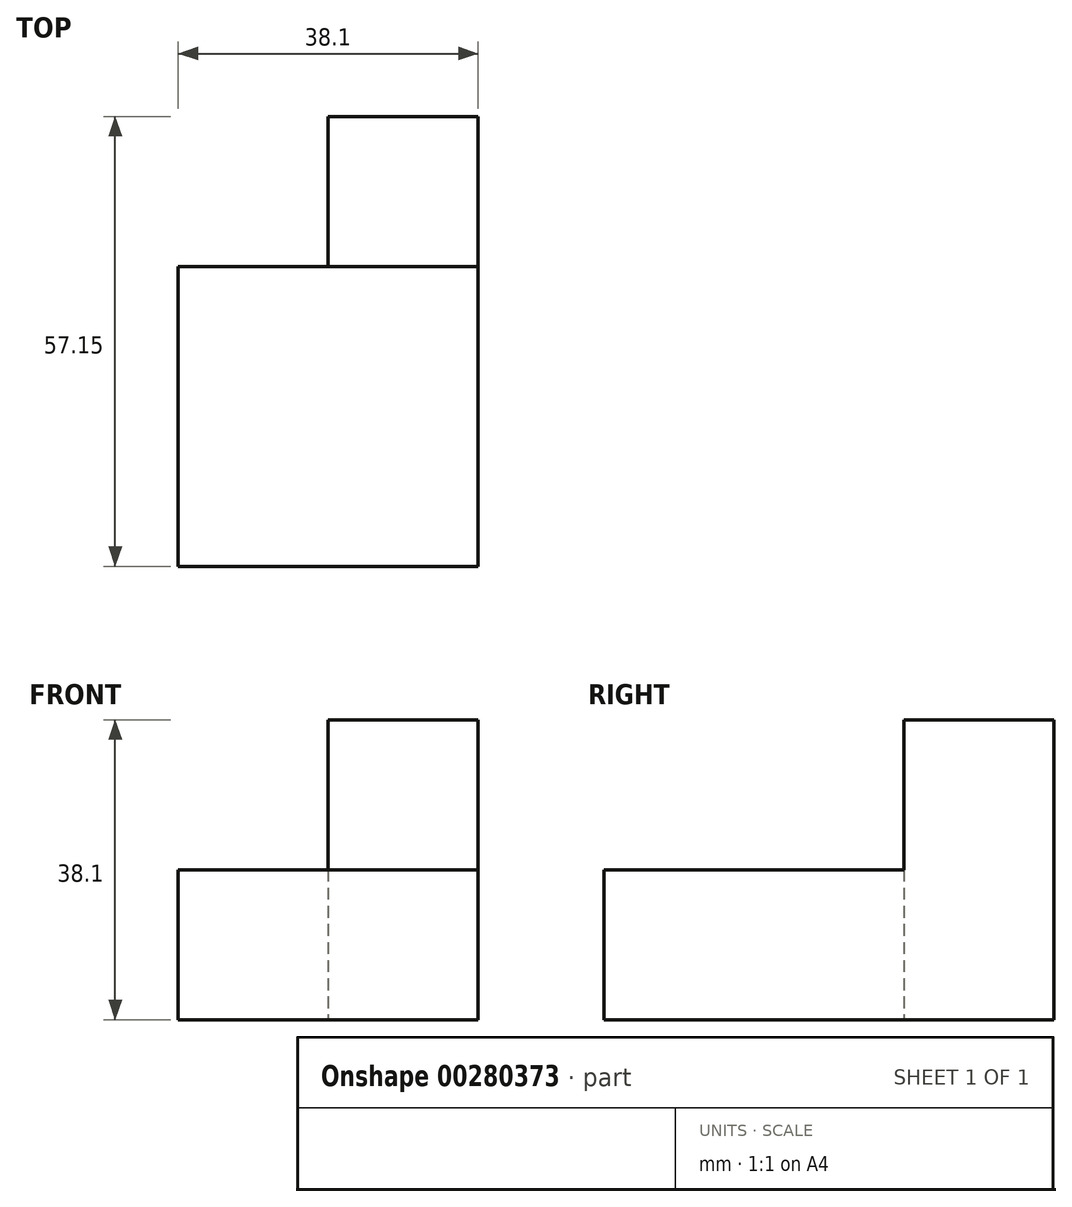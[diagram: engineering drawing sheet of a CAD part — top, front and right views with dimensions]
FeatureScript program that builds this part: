
annotation { "Feature Type Name" : "Feature", "Feature Type Description" : "" }
export const myFeature = defineFeature(function(context is Context, id is Id, definition is map)
    precondition{}
    {
        {
            var Q0;
            Q0=qCreatedBy(makeId("Top.planeOp"),FACE);
            var sketch = newSketch(context, id + "F0", { "sketchPlane" : qUnion([Q0])});
            skLineSegment(sketch, "E0.bottom", {"start": v(0, 0) * mm, "end": v(38.1, 0) * mm});
            skLineSegment(sketch, "E0.top", {"start": v(0, 38.1) * mm, "end": v(19.05, 38.1) * mm});
            skLineSegment(sketch, "E0.left", {"start": v(0, 0) * mm, "end": v(0, 38.1) * mm});
            skLineSegment(sketch, "E0.right", {"start": v(38.1, 0) * mm, "end": v(38.1, 38.1) * mm});
            skLineSegment(sketch, "E1", {"start": v(19.05, 38.1) * mm, "end": v(19.05, 57.15) * mm});
            skLineSegment(sketch, "E2", {"start": v(19.05, 57.15) * mm, "end": v(38.1, 57.15) * mm});
            skLineSegment(sketch, "E3", {"start": v(38.1, 57.15) * mm, "end": v(38.1, 38.1) * mm});
            skSolve(sketch);
        }
        {
            var Q0;
            Q0 = qSketchRegion(id + "F0", true);
            extrude(context, id + "F1", {"entities" : qUnion([Q0]), "depth" : 19.05 * mm});
        }
        {
            var Q0;
            Q0=makeQuery(id+"F1.opExtrude","CAP_FACE",FACE,{"disambiguationData":[OSD([sQuery(id+"F0.wireOp",EDGE,"E0.bottom"),sQuery(id+"F0.wireOp",EDGE,"E0.top"),sQuery(id+"F0.wireOp",EDGE,"E0.left"),sQuery(id+"F0.wireOp",EDGE,"E0.right"),sQuery(id+"F0.wireOp",EDGE,"E1"),sQuery(id+"F0.wireOp",EDGE,"E2"),sQuery(id+"F0.wireOp",EDGE,"E3")])],"isStart":false});
            var sketch = newSketch(context, id + "F2", { "sketchPlane" : qUnion([Q0])});
            skLineSegment(sketch, "E4.bottom", {"start": v(19.05, 38.1) * mm, "end": v(38.1, 38.1) * mm});
            skLineSegment(sketch, "E4.top", {"start": v(19.05, 57.15) * mm, "end": v(38.1, 57.15) * mm});
            skLineSegment(sketch, "E4.left", {"start": v(19.05, 38.1) * mm, "end": v(19.05, 57.15) * mm});
            skLineSegment(sketch, "E4.right", {"start": v(38.1, 38.1) * mm, "end": v(38.1, 57.15) * mm});
            skSolve(sketch);
        }
        {
            var Q0;
            Q0 = qSketchRegion(id + "F2", true);
            extrude(context, id + "F3", {"entities" : qUnion([Q0]), "operationType" : NewBodyOperationType.ADD, "depth" : 19.05 * mm});
        }
    });
